# Revit family: 0043327 Feilo Sylvania Lighting Fixture CONVENIO LINEAR SP 12V 3000K L400 KIT EU
name_source: partatom
category: Lighting Fixtures
revit_build: Autodesk Revit 2017 (Build: 20190507_1515(x64)
units: mm (PartAtom-declared; Revit-internal decimal feet)

## family parameters
Cut with Voids When Loaded = No
Host = Face
Light Source = No
OmniClass Number = 23.80.70.00
OmniClass Title = Lighting
Part Type = Normal
Room Calculation Point = No
Round Connector Dimension = Use Diameter
Shared = No

## types (1)
- 0043327 CONVENIO LINEAR SP 12V 3000K L400 KIT EU
    Apparent Load = 9 VA
    Assembly Code = D5020200
    AssetType = Fixed
    ClassificationName = Uniclass2015
    ClassificationValue = EF_70_80
    Cost = 0 $
    Default Elevation = 1219 mm
    Description = LED linear spot striplight, 600LM, 8.5W, L400, 3000K, 3 x LED spots with 25 degree beam angle, includes driver and EU plug, white/silver aluminium body, low slimline profile, dimensions length 400mm, width 30mm, height 15mm, expandable with accessories, IP20.  14.4W LED Driver is included in the packaging.
    DocumentationLiterature = http://www.sylvania-lighting.com
    DurationUnit = hours
    ElectricShockClassification = Class II
    ExpectedLife = 50000
    IfcExportAs = IfcLightFixtureType
    IfcExportType = IfcLightFixtureType
    IngressProtection = IP20
    InputVoltage = 220-240V~
    Keynote = 16500
    Lamp = LED
    LampColourRenderingIndex = 0
    LampColourTemperature = 3000 K
    LampNominalLuminous = 600 lm
    LampsType = LED
    Length_FEILO = 400 mm  [stored 1.31234 ft]
    LightsOffset_FEILO = 67 mm
    LuminousEfficacy = 70 lm/W
    Manufacturer = Feilo Sylvania
    ManufacturerName = Feilo Sylvania
    Material = aluminium housing
    Material_1_FEILO = Body-Sylvania-Convenio Spot-White
    Material_2_FEILO = Diffuser-Sylvania-Convenio Spot
    Material_3_FEILO = <By Category>
    Material_4_FEILO = <By Category>
    Model = CONVENIO LINEAR SP 12V 3000K L400 KIT EU
    ModelNumber = 0043327
    ModelReference = CONVENIO LINEAR SP 12V 3000K L400 KIT EU
    Name = CONVENIO LINEAR SP 12V 3000K L400 KIT EU
    NominalDepth = 30 mm  [stored 0.0984252 ft]
    NominalHeight = 15 mm  [stored 0.0492126 ft]
    NominalLength = 400 mm  [stored 1.31234 ft]
    PowerConsumption = 8.5 W
    PowerFactor = 0
    Type Image = <None>
    TypeName = CONVENIO LINEAR SP 12V 3000K L400 KIT EU
    URL = http://www.sylvania-lighting.com
    Voltage = 230 V
    Weight = 6.54 kg

note: [stored X ft] marks values corroborated as IEEE doubles in the binary element streams (Revit-internal decimal feet)

## geometry (parser evidence)
native form markers: Sweep x3
no freeform markers — native parametric forms only
